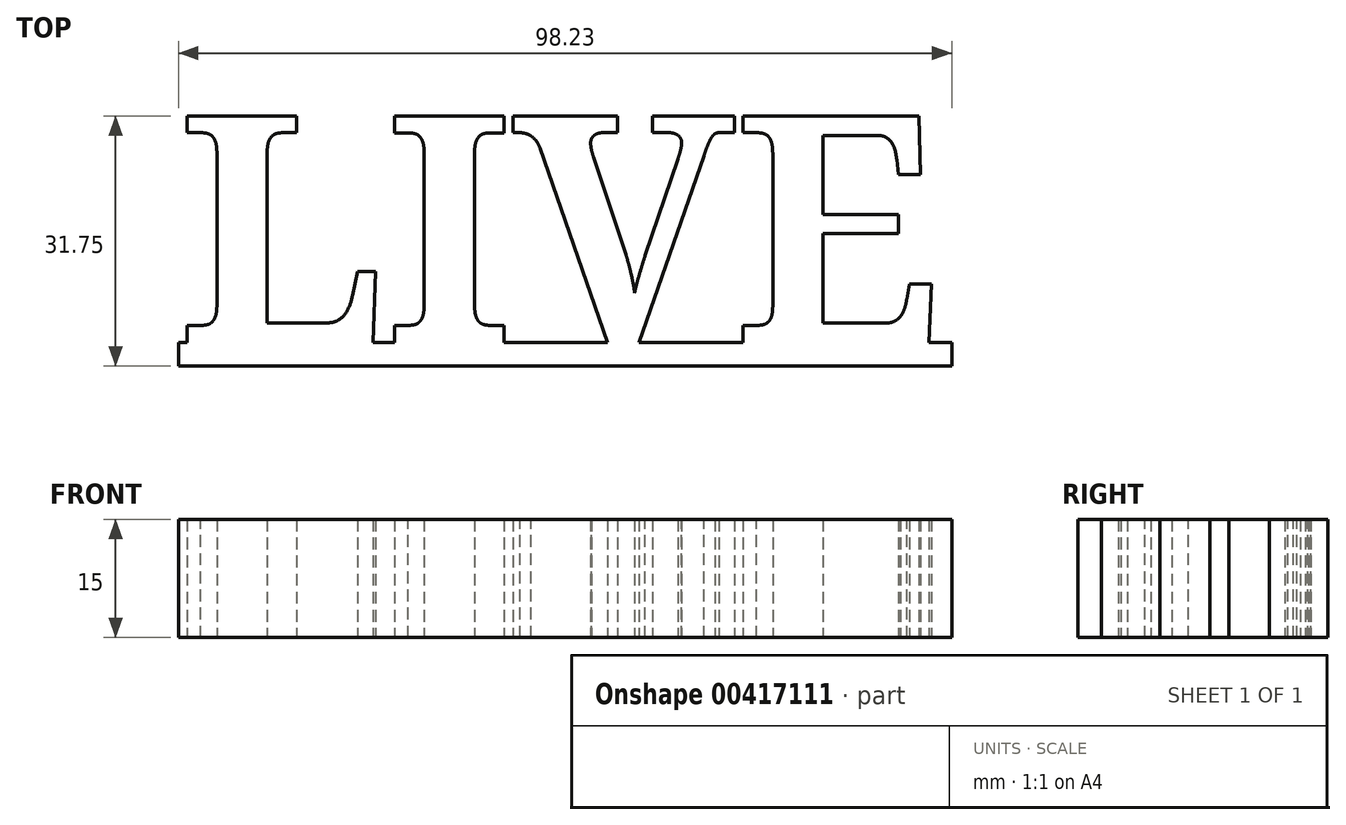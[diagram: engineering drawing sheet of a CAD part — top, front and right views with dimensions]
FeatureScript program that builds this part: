
annotation { "Feature Type Name" : "Feature", "Feature Type Description" : "" }
export const myFeature = defineFeature(function(context is Context, id is Id, definition is map)
    precondition{}
    {
        {
            var Q0;
            Q0=qCreatedBy(makeId("Top.planeOp"),FACE);
            var sketch = newSketch(context, id + "F0", { "sketchPlane" : qUnion([Q0])});
            skText(sketch, "E0", { "text": "LIVE", "fontName": "NotoSerif-Bold.ttf"});
            skLineSegment(sketch, "E1", {"start": v(0, 0) * mm, "end": v(24.92, 0) * mm});
            skLineSegment(sketch, "E2", {"start": v(0, 0) * mm, "end": v(98.23, 0) * mm});
            skLineSegment(sketch, "E3", {"start": v(98.23, -3) * mm, "end": v(0, -3) * mm});
            skLineSegment(sketch, "E4", {"start": v(0, -3) * mm, "end": v(0, 0) * mm});
            skLineSegment(sketch, "E5", {"start": v(98.23, -3) * mm, "end": v(98.23, 0) * mm});
            const initialGuessF0  = {"E0": [0, 0, 1, 0, 0.029]};
            skSetInitialGuess(sketch, initialGuessF0);
            skSolve(sketch);
        }
        {
            var Q0;
            Q0 = qSketchRegion(id + "F0", true);
            extrude(context, id + "F1", {"entities" : qUnion([Q0]), "depth" : 15 * mm});
        }
    });
